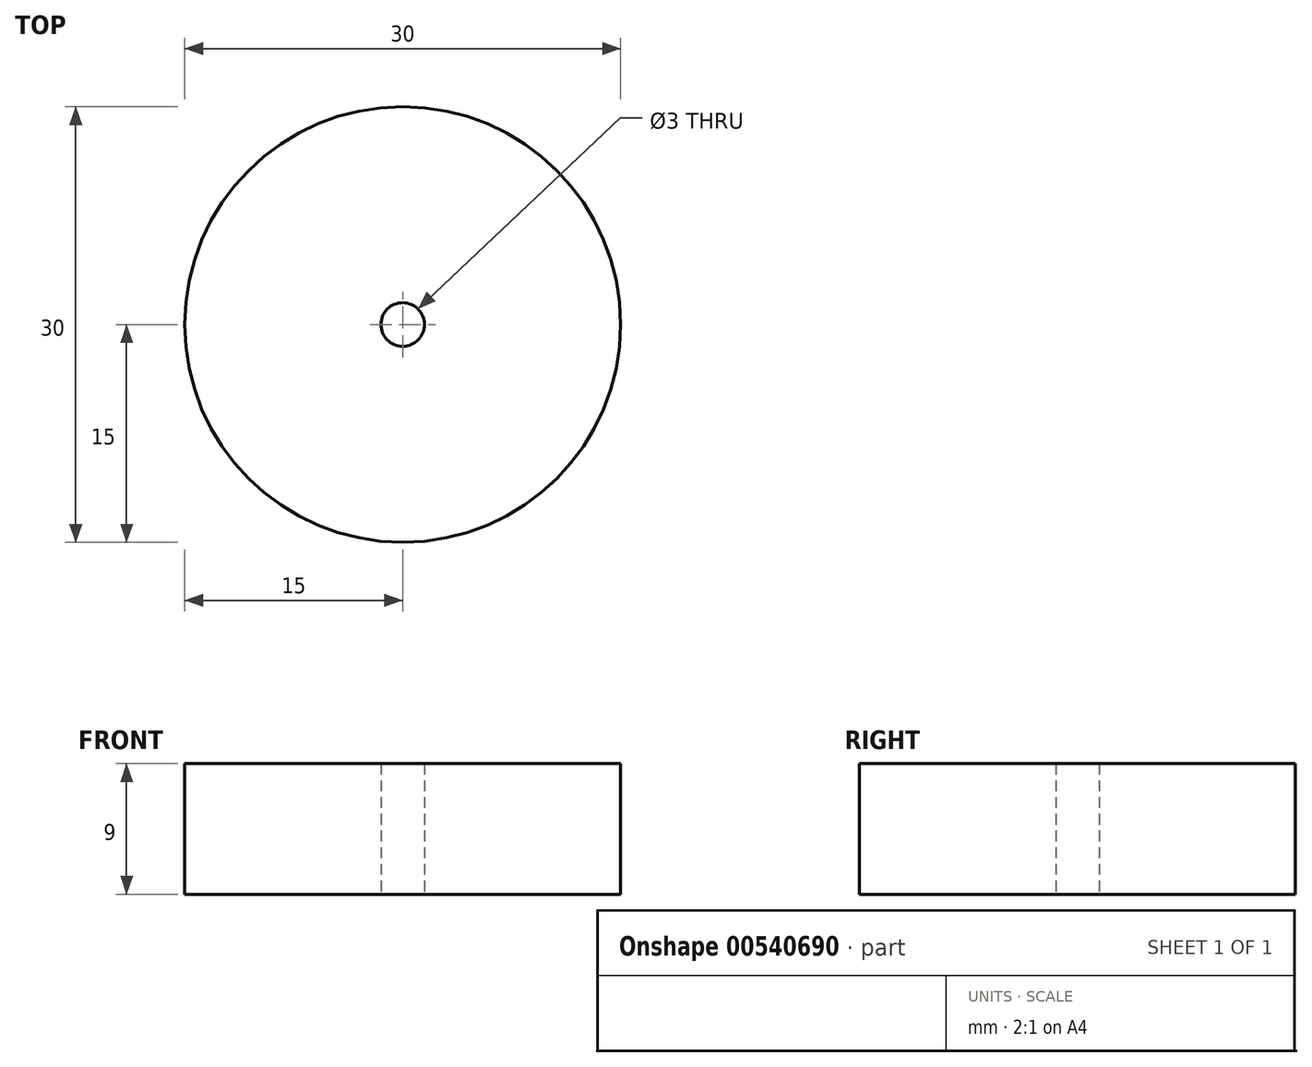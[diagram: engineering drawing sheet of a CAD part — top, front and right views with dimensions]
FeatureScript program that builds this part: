
annotation { "Feature Type Name" : "Feature", "Feature Type Description" : "" }
export const myFeature = defineFeature(function(context is Context, id is Id, definition is map)
    precondition{}
    {
        {
            var Q0;
            Q0=qCreatedBy(makeId("Top.planeOp"),FACE);
            var sketch = newSketch(context, id + "F0", { "sketchPlane" : qUnion([Q0])});
            skCircle(sketch, "E0", {"center": v(0, 0) * mm, "radius": 1.5 * mm});
            skCircle(sketch, "E1", {"center": v(0, 0) * mm, "radius": 15 * mm});
            skSolve(sketch);
        }
        {
            var Q0;
            Q0=qSketchRegion(id+"F0",true);
            extrude(context, id + "F1", {"entities" : qUnion([Q0]), "depth" : 9 * mm});
        }
    });
